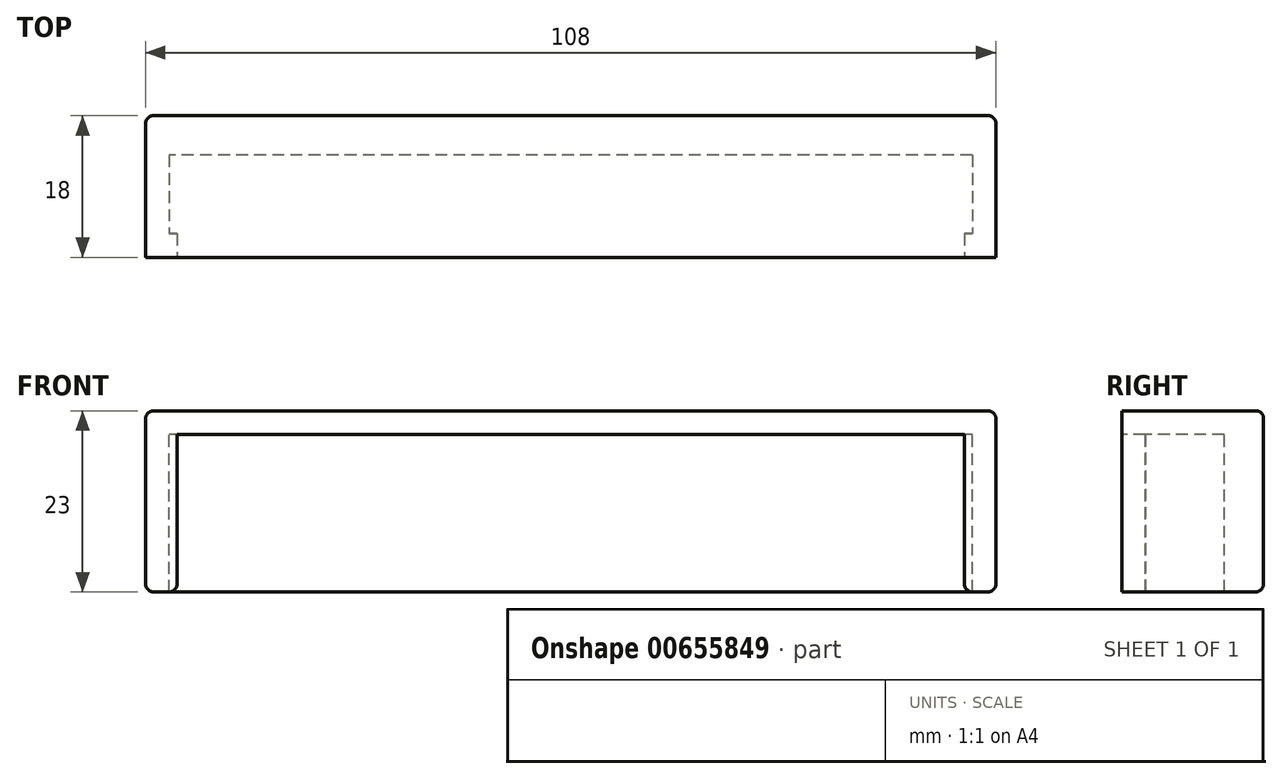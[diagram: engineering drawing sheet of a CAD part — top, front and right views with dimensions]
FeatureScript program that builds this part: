
annotation { "Feature Type Name" : "Feature", "Feature Type Description" : "" }
export const myFeature = defineFeature(function(context is Context, id is Id, definition is map)
    precondition{}
    {
        {
            var Q0;
            Q0=qCreatedBy(makeId("Front.planeOp"),FACE);
            var sketch = newSketch(context, id + "F0", { "sketchPlane" : qUnion([Q0])});
            skLineSegment(sketch, "E0.bottom", {"start": v(51, 0) * mm, "end": v(-51, 0) * mm});
            skLineSegment(sketch, "E0.top", {"start": v(51, 20) * mm, "end": v(-51, 20) * mm});
            skLineSegment(sketch, "E0.left", {"start": v(51, 0) * mm, "end": v(51, 20) * mm});
            skLineSegment(sketch, "E0.right", {"start": v(-51, 0) * mm, "end": v(-51, 20) * mm});
            skPoint(sketch, "E0.middle", {"position": v(0, 10) * mm});
            skLineSegment(sketch, "E1", {"start": v(-50, 20) * mm, "end": v(-50, 0) * mm});
            skLineSegment(sketch, "E2", {"start": v(50, 20) * mm, "end": v(50, 0) * mm});
            skLineSegment(sketch, "E3.0", {"start": v(-54, 0) * mm, "end": v(-54, 23) * mm});
            skLineSegment(sketch, "E3.1", {"start": v(54, 23) * mm, "end": v(-54, 23) * mm});
            skLineSegment(sketch, "E3.2", {"start": v(54, 0) * mm, "end": v(54, 23) * mm});
            skLineSegment(sketch, "E4", {"start": v(-54, 0) * mm, "end": v(-51, 0) * mm});
            skLineSegment(sketch, "E5", {"start": v(51, 0) * mm, "end": v(54, 0) * mm});
            skSolve(sketch);
        }
        {
            var Q0;
            {var subQ0=sQuery(id+"F0.wireOp",EDGE,"E0.left");Q0=makeQuery(id+"F0.imprint","IMPRINT",FACE,{"disambiguationData":[TD([[makeQuery(id+"F0.imprint","IMPRINT",EDGE,{"derivedFrom":subQ0}),-1.0]])]});}
            var Q1;
            {var subQ0=sQuery(id+"F0.wireOp",EDGE,"E0.right");Q1=makeQuery(id+"F0.imprint","IMPRINT",FACE,{"disambiguationData":[TD([[makeQuery(id+"F0.imprint","IMPRINT",EDGE,{"derivedFrom":subQ0}),-1.0]])]});}
            var Q2;
            {var subQ0=sQuery(id+"F0.wireOp",EDGE,"E1");Q2=makeQuery(id+"F0.imprint","IMPRINT",FACE,{"disambiguationData":[TD([[makeQuery(id+"F0.imprint","IMPRINT",EDGE,{"derivedFrom":subQ0}),1.0]])]});}
            var Q3;
            {var subQ0=sQuery(id+"F0.wireOp",EDGE,"E0.left");Q3=makeQuery(id+"F0.imprint","IMPRINT",FACE,{"disambiguationData":[TD([[makeQuery(id+"F0.imprint","IMPRINT",EDGE,{"derivedFrom":subQ0}),1.0]])]});}
            extrude(context, id + "F1", {"entities" : qUnion([Q0, Q1, Q2, Q3]), "oppositeDirection" : true, "depth" : 18 * mm, "offsetDistance" : 25 * mm});
        }
        {
            var Q0;
            {var subQ0=sQuery(id+"F0.wireOp",EDGE,"E0.right");Q0=makeQuery(id+"F0.imprint","IMPRINT",FACE,{"disambiguationData":[TD([[makeQuery(id+"F0.imprint","IMPRINT",EDGE,{"derivedFrom":subQ0}),-1.0]])]});}
            var Q1;
            {var subQ0=sQuery(id+"F0.wireOp",EDGE,"E1");Q1=makeQuery(id+"F0.imprint","IMPRINT",FACE,{"disambiguationData":[TD([[makeQuery(id+"F0.imprint","IMPRINT",EDGE,{"derivedFrom":subQ0}),1.0]])]});}
            var Q2;
            {var subQ0=sQuery(id+"F0.wireOp",EDGE,"E0.left");Q2=makeQuery(id+"F0.imprint","IMPRINT",FACE,{"disambiguationData":[TD([[makeQuery(id+"F0.imprint","IMPRINT",EDGE,{"derivedFrom":subQ0}),1.0]])]});}
            extrude(context, id + "F2", {"entities" : qUnion([Q0, Q1, Q2]), "operationType" : NewBodyOperationType.REMOVE, "oppositeDirection" : true, "depth" : 13 * mm, "offsetDistance" : 25 * mm});
        }
        {
            var Q0;
            {var subQ0=sQuery(id+"F0.wireOp",EDGE,"E0.right");Q0=makeQuery(id+"F0.imprint","IMPRINT",FACE,{"disambiguationData":[TD([[makeQuery(id+"F0.imprint","IMPRINT",EDGE,{"derivedFrom":subQ0}),-1.0]])]});}
            var Q1;
            {var subQ0=sQuery(id+"F0.wireOp",EDGE,"E0.left");Q1=makeQuery(id+"F0.imprint","IMPRINT",FACE,{"disambiguationData":[TD([[makeQuery(id+"F0.imprint","IMPRINT",EDGE,{"derivedFrom":subQ0}),1.0]])]});}
            extrude(context, id + "F3", {"entities" : qUnion([Q0, Q1]), "operationType" : NewBodyOperationType.ADD, "oppositeDirection" : true, "depth" : 3 * mm, "offsetDistance" : 25 * mm});
        }
        {
            var Q0;
            Q0=makeQuery(id+"F1.opExtrude","CAP_EDGE",EDGE,{"disambiguationData":[OSD([sQuery(id+"F0.wireOp",EDGE,"E3.0")])],"isStart":false});
            var Q1;
            Q1=makeQuery(id+"F1.opExtrude","CAP_EDGE",EDGE,{"disambiguationData":[OSD([sQuery(id+"F0.wireOp",EDGE,"E3.2")])],"isStart":false});
            var Q2;
            Q2=makeQuery(id+"F1.opExtrude","CAP_EDGE",EDGE,{"disambiguationData":[OSD([sQuery(id+"F0.wireOp",EDGE,"E0.bottom"),sQuery(id+"F0.wireOp",EDGE,"E4"),sQuery(id+"F0.wireOp",EDGE,"E5")])],"isStart":false});
            var Q3;
            Q3=makeQuery(id+"F1.opExtrude","SWEPT_EDGE",EDGE,{"disambiguationData":[OSD([sQuery(id+"F0.wireOp",EDGE,"E3.2"),sQuery(id+"F0.wireOp",EDGE,"E5")])]});
            var Q4;
            Q4=makeQuery(id+"F1.opExtrude","SWEPT_EDGE",EDGE,{"disambiguationData":[OSD([sQuery(id+"F0.wireOp",EDGE,"E3.0"),sQuery(id+"F0.wireOp",EDGE,"E4")])]});
            var Q5;
            Q5=makeQuery(id+"F1.opExtrude","SWEPT_EDGE",EDGE,{"disambiguationData":[OSD([sQuery(id+"F0.wireOp",EDGE,"E3.0"),sQuery(id+"F0.wireOp",EDGE,"E3.1")])]});
            var Q6;
            Q6=makeQuery(id+"F1.opExtrude","CAP_EDGE",EDGE,{"disambiguationData":[OSD([sQuery(id+"F0.wireOp",EDGE,"E3.1")])],"isStart":false});
            var Q7;
            Q7=makeQuery(id+"F1.opExtrude","SWEPT_EDGE",EDGE,{"disambiguationData":[OSD([sQuery(id+"F0.wireOp",EDGE,"E3.1"),sQuery(id+"F0.wireOp",EDGE,"E3.2")])]});
            var Q8;
            Q8=makeQuery(id+"F2.boolean.opBoolean","COPY",EDGE,{"derivedFrom":makeQuery(id+"F2.opExtrude","CAP_EDGE",EDGE,{"disambiguationData":[OSD([sQuery(id+"F0.wireOp",EDGE,"E0.bottom")])],"isStart":false})});
            var Q9;
            Q9=makeQuery(id+"F2.boolean.opBoolean","COPY",EDGE,{"derivedFrom":makeQuery(id+"F2.opExtrude","SWEPT_EDGE",EDGE,{"disambiguationData":[OSD([sQuery(id+"F0.wireOp",EDGE,"E0.bottom"),sQuery(id+"F0.wireOp",EDGE,"E0.left"),sQuery(id+"F0.wireOp",EDGE,"E5")])]})});
            var Q10;
            Q10=makeQuery(id+"F2.boolean.opBoolean","COPY",EDGE,{"derivedFrom":makeQuery(id+"F2.opExtrude","SWEPT_EDGE",EDGE,{"disambiguationData":[OSD([sQuery(id+"F0.wireOp",EDGE,"E0.bottom"),sQuery(id+"F0.wireOp",EDGE,"E0.right"),sQuery(id+"F0.wireOp",EDGE,"E4")])]})});
            var Q11;
            Q11=makeQuery(id+"F3.opExtrude","SWEPT_EDGE",EDGE,{"disambiguationData":[OSD([sQuery(id+"F0.wireOp",EDGE,"E0.bottom"),sQuery(id+"F0.wireOp",EDGE,"E1")])]});
            var Q12;
            Q12=makeQuery(id+"F3.opExtrude","SWEPT_EDGE",EDGE,{"disambiguationData":[OSD([sQuery(id+"F0.wireOp",EDGE,"E0.bottom"),sQuery(id+"F0.wireOp",EDGE,"E2")])]});
            fillet(context, id + "F4", {"entities" : qUnion([Q0, Q1, Q2, Q3, Q4, Q5, Q6, Q7, Q8, Q9, Q10, Q11, Q12]), "radius" : 1 * mm, "tangentPropagation" : true, "allowEdgeOverflow" : false});
        }
    });
